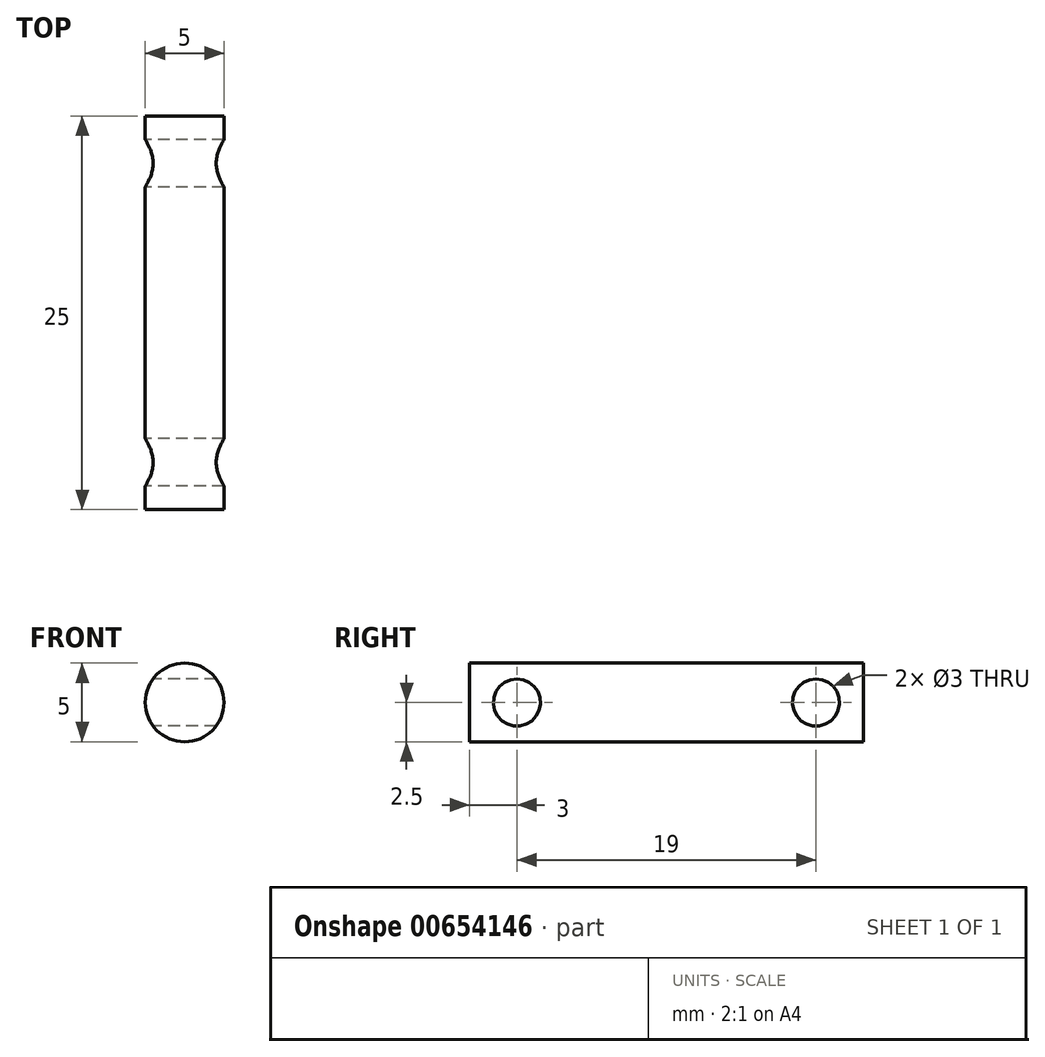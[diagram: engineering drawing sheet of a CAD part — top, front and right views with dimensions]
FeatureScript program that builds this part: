
annotation { "Feature Type Name" : "Feature", "Feature Type Description" : "" }
export const myFeature = defineFeature(function(context is Context, id is Id, definition is map)
    precondition{}
    {
        {
            var Q0;
            Q0=qCreatedBy(makeId("Front.planeOp"),FACE);
            var sketch = newSketch(context, id + "F0", { "sketchPlane" : qUnion([Q0])});
            skCircle(sketch, "E0", {"center": v(0, 0) * mm, "radius": 2.5 * mm});
            skSolve(sketch);
        }
        {
            var Q0;
            Q0 = qSketchRegion(id + "F0", true);
            extrude(context, id + "F1", {"entities" : qUnion([Q0]), "depth" : 25 * mm, "offsetDistance" : 25 * mm});
        }
        {
            var Q0;
            Q0=qCreatedBy(makeId("Right.planeOp"),FACE);
            var sketch = newSketch(context, id + "F2", { "sketchPlane" : qUnion([Q0])});
            skCircle(sketch, "E1", {"center": v(-3, 0) * mm, "radius": 1.5 * mm});
            skCircle(sketch, "E2", {"center": v(-22, 0) * mm, "radius": 1.5 * mm});
            skSolve(sketch);
        }
        {
            var Q0;
            Q0 = qSketchRegion(id + "F2", true);
            extrude(context, id + "F3", {"entities" : qUnion([Q0]), "operationType" : NewBodyOperationType.REMOVE, "depth" : 5 * mm, "offsetDistance" : 25 * mm, "hasSecondDirection" : true, "secondDirectionOppositeDirection" : true, "secondDirectionDepth" : 5 * mm});
        }
    });
